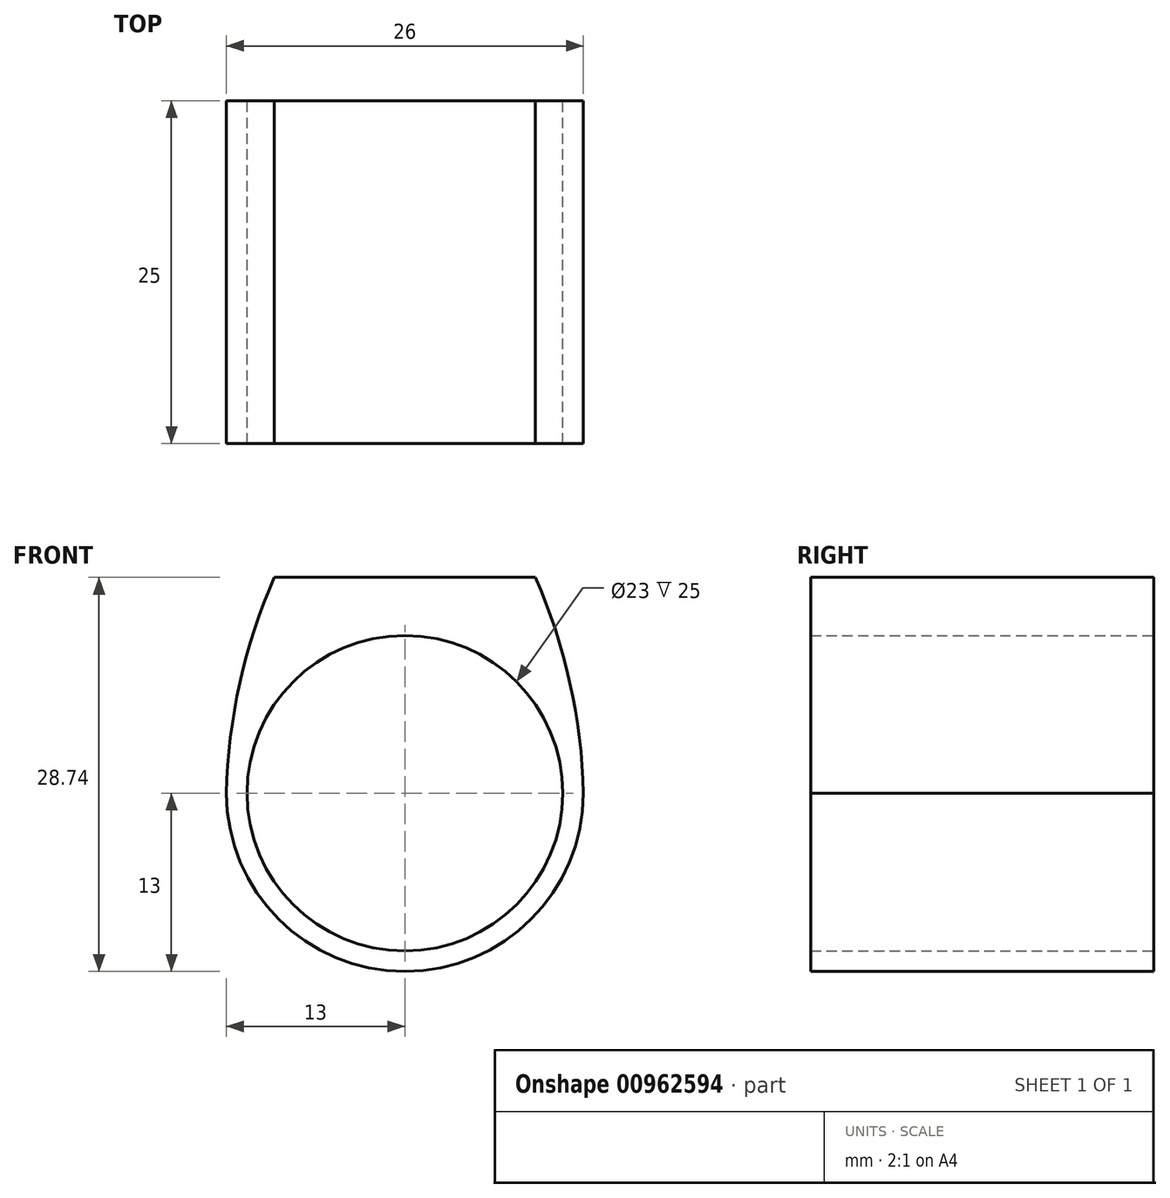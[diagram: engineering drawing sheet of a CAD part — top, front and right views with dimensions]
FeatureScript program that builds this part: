
annotation { "Feature Type Name" : "Feature", "Feature Type Description" : "" }
export const myFeature = defineFeature(function(context is Context, id is Id, definition is map)
    precondition{}
    {
        {
            var Q0;
            Q0=qCreatedBy(makeId("Front.planeOp"),FACE);
            var sketch = newSketch(context, id + "F0", { "sketchPlane" : qUnion([Q0])});
            skCircle(sketch, "E0", {"center": v(0, 0) * mm, "radius": 11.5 * mm});
            skCircle(sketch, "E1", {"center": v(0, 0) * mm, "radius": 13 * mm});
            skLineSegment(sketch, "E2.bottom", {"start": v(-9.5, 0) * mm, "end": v(9.5, 0) * mm});
            skLineSegment(sketch, "E2.top", {"start": v(-9.5, 15.74) * mm, "end": v(9.5, 15.74) * mm});
            skLineSegment(sketch, "E2.left", {"start": v(-9.5, 0) * mm, "end": v(-9.5, 15.74) * mm});
            skLineSegment(sketch, "E2.right", {"start": v(9.5, 0) * mm, "end": v(9.5, 15.74) * mm});
            skArc(sketch, "E3", {"start": v(13, 0) * mm, "mid": v(12.03, 8.04) * mm, "end": v(9.5, 15.74) * mm});
            skArc(sketch, "E4.MirrorCS", {"start": v(-13, 0) * mm, "mid": v(-12.03, 8.04) * mm, "end": v(-9.5, 15.74) * mm});
            skSolve(sketch);
        }
        {
            var Q0;
            {var subQ5=sQuery(id+"F0.wireOp",EDGE,"E2.top");Q0=makeQuery(id+"F0.imprint","IMPRINT",FACE,{"disambiguationData":[TD([[makeQuery(id+"F0.imprint","IMPRINT",EDGE,{"derivedFrom":subQ5}),-1.0]])]});}
            var Q1;
            {var subQ0=sQuery(id+"F0.wireOp",EDGE,"E2.left");var subQ1=sQuery(id+"F0.wireOp",EDGE,"E0");var subQ2=makeQuery(id+"F0.imprint","INTERSECT",VERTEX,{"derivedFrom":[subQ1,subQ0]});Q1=makeQuery(id+"F0.imprint","IMPRINT",FACE,{"disambiguationData":[TD([[makeQuery(id+"F0.imprint","IMPRINT",EDGE,{"disambiguationData":[TD([[subQ2,1.0]])],"derivedFrom":subQ1}),-1.0]])]});}
            var Q2;
            {var subQ0=sQuery(id+"F0.wireOp",EDGE,"E4.MirrorCS");var subQ1=sQuery(id+"F0.wireOp",EDGE,"E1");var subQ2=makeQuery(id+"F0.imprint","INTERSECT",VERTEX,{"disambiguationData":[OD(1.0)],"derivedFrom":[subQ1,subQ0]});Q2=makeQuery(id+"F0.imprint","IMPRINT",FACE,{"disambiguationData":[TD([[makeQuery(id+"F0.imprint","IMPRINT",EDGE,{"disambiguationData":[TD([[subQ2,1.0]])],"derivedFrom":subQ1}),-1.0]])]});}
            var Q3;
            {var subQ6=sQuery(id+"F0.wireOp",EDGE,"E2.left");var subQ11=sQuery(id+"F0.wireOp",EDGE,"E0");var subQ13=makeQuery(id+"F0.imprint","INTERSECT",VERTEX,{"derivedFrom":[subQ11,subQ6]});Q3=makeQuery(id+"F0.imprint","IMPRINT",FACE,{"disambiguationData":[TD([[makeQuery(id+"F0.imprint","IMPRINT",EDGE,{"disambiguationData":[TD([[subQ13,-1.0]])],"derivedFrom":subQ11}),-1.0]])]});}
            var Q4;
            {var subQ0=sQuery(id+"F0.wireOp",EDGE,"E3");var subQ1=sQuery(id+"F0.wireOp",EDGE,"E1");var subQ2=makeQuery(id+"F0.imprint","INTERSECT",VERTEX,{"disambiguationData":[OD(1.0)],"derivedFrom":[subQ1,subQ0]});Q4=makeQuery(id+"F0.imprint","IMPRINT",FACE,{"disambiguationData":[TD([[makeQuery(id+"F0.imprint","IMPRINT",EDGE,{"disambiguationData":[TD([[subQ2,-1.0]])],"derivedFrom":subQ1}),-1.0]])]});}
            extrude(context, id + "F1", {"entities" : qUnion([Q0, Q1, Q2, Q3, Q4]), "depth" : 25 * mm, "offsetDistance" : 25 * mm});
        }
        {
            var Q0;
            Q0=qCreatedBy(makeId("Right.planeOp"),FACE);
            cPlane(context, id + "F2", {"entities" : qUnion([Q0]), "cplaneType" : CPlaneType.OFFSET, "offset" : 15 * mm, "width" : 150 * mm, "height" : 150 * mm});
        }
    });
